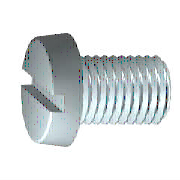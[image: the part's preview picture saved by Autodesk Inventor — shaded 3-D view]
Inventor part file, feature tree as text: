
AUTODESK INVENTOR PART (.ipt)
format: ipt  version: 2015 (Build 190159000, 159)  size: 185,856 bytes
history: native  units: mm (DEFAULTED — no unit token found)
features: sketch x2, extrude x1, plane x1
ambient origin geometry x7: Origin, YZ Plane, XZ Plane, X Axis, Y Axis, Z Axis, Center Point
bodies: Solid1 (feature_tree), Body (feature_tree)
feature tree (4):
  sketch  "Sketch2"  dims[d2=0.36817mm d3=2.4mm d4=3.5mm d5=3.17524mm d8=90.0deg d7=0.0mm d9=6.0mm d10=0.872665mm d11=1.0mm d12=6.0mm d14=0.1mm d15=3.8mm d16=0.0mm d17=0.32476mm d18=0.36817mm d19=1.0mm d20=0.0mm d36=45.0deg d37=0.0mm d39=0.0mm]
  extrude  "Slot"  Depth=3.8mm
  plane  "Work Plane1"
  sketch  "Sketch1"  dims[d0=5.0mm d1=3.8mm]
